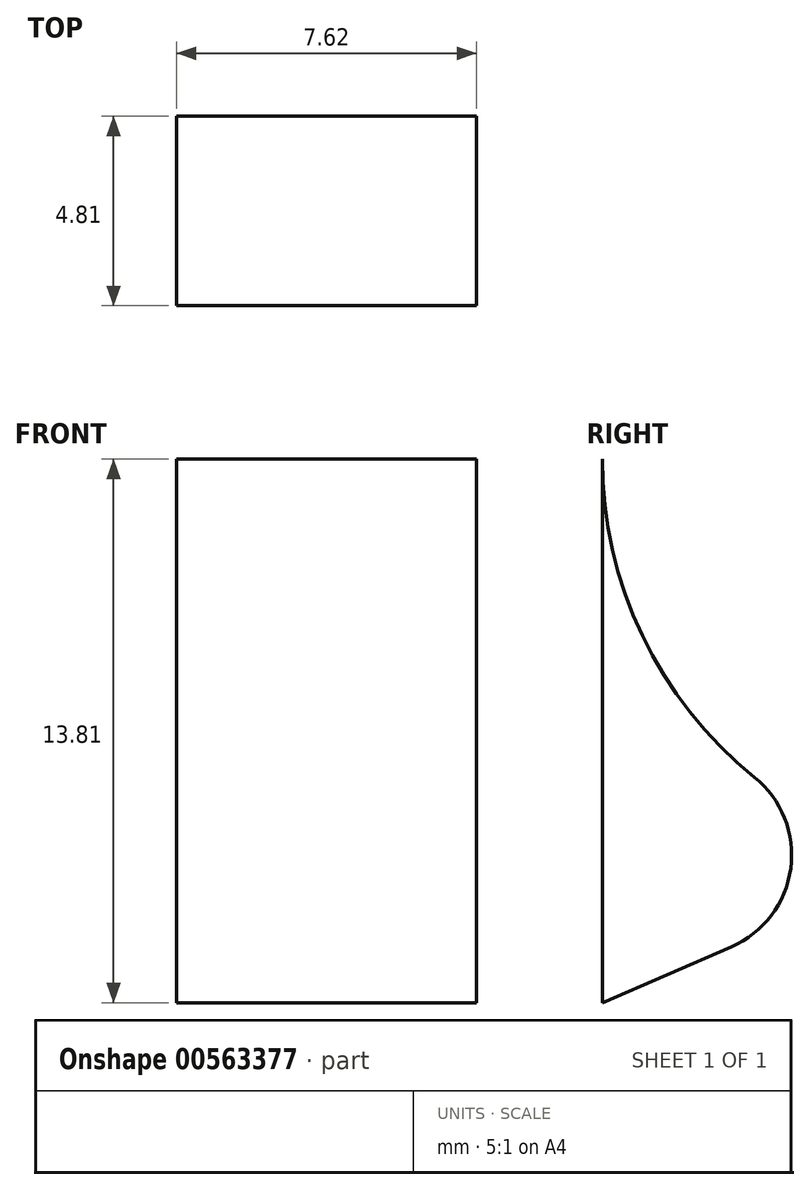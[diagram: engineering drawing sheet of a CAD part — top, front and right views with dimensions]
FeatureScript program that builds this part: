
annotation { "Feature Type Name" : "Feature", "Feature Type Description" : "" }
export const myFeature = defineFeature(function(context is Context, id is Id, definition is map)
    precondition{}
    {
        {
            var Q0;
            Q0=qCreatedBy(makeId("Right.planeOp"),FACE);
            var sketch = newSketch(context, id + "F0", { "sketchPlane" : qUnion([Q0])});
            skLineSegment(sketch, "E0", {"start": v(-43.53, 35.96) * mm, "end": v(-43.53, 22.15) * mm});
            skLineSegment(sketch, "E1", {"start": v(-43.53, 22.15) * mm, "end": v(-35.16, 25.77) * mm});
            skArc(sketch, "E2", {"start": v(-43.53, 35.96) * mm, "mid": v(-41.17, 29.37) * mm, "end": v(-35.16, 25.77) * mm});
            skSolve(sketch);
        }
        {
            var Q0;
            Q0=qSketchRegion(id+"F0",true);
            extrude(context, id + "F1", {"entities" : qUnion([Q0]), "depth" : 7.62 * mm});
        }
        {
            var Q0;
            Q0=makeQuery(id+"F1.opExtrude","SWEPT_EDGE",EDGE,{"disambiguationData":[OSD([sQuery(id+"F0.wireOp",EDGE,"E1"),sQuery(id+"F0.wireOp",EDGE,"E2")])]});
            fillet(context, id + "F2", {"entities" : qUnion([Q0]), "radius" : 2.54 * mm, "tangentPropagation" : true, "allowEdgeOverflow" : false});
        }
    });
